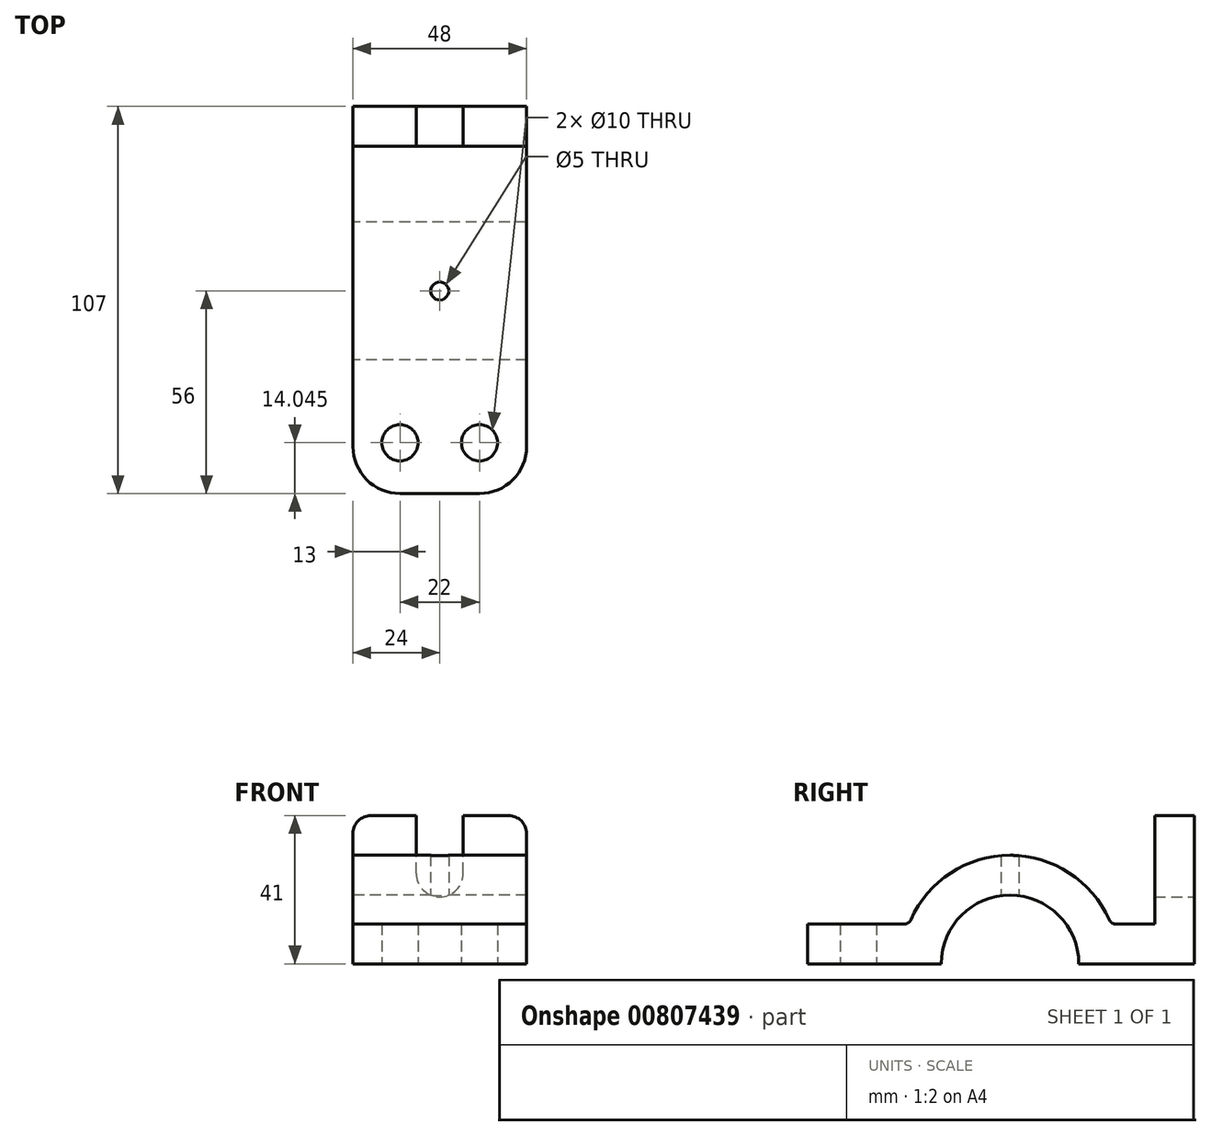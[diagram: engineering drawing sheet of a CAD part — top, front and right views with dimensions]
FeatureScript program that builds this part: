
annotation { "Feature Type Name" : "Feature", "Feature Type Description" : "" }
export const myFeature = defineFeature(function(context is Context, id is Id, definition is map)
    precondition{}
    {
        {
            var Q0;
            Q0=qCreatedBy(makeId("Right.planeOp"),FACE);
            var sketch = newSketch(context, id + "F0", { "sketchPlane" : qUnion([Q0])});
            skCircle(sketch, "E0", {"center": v(0, 0) * mm, "radius": 19 * mm});
            skCircle(sketch, "E1", {"center": v(0, 0) * mm, "radius": 30 * mm});
            skLineSegment(sketch, "E2.bottom", {"start": v(-56, 0) * mm, "end": v(51, 0) * mm});
            skLineSegment(sketch, "E2.top", {"start": v(-56, 11) * mm, "end": v(51, 11) * mm});
            skLineSegment(sketch, "E2.left", {"start": v(-56, 0) * mm, "end": v(-56, 11) * mm});
            skLineSegment(sketch, "E2.right", {"start": v(51, 0) * mm, "end": v(51, 11) * mm});
            skLineSegment(sketch, "E3.bottom", {"start": v(51, 11) * mm, "end": v(40, 11) * mm});
            skLineSegment(sketch, "E3.top", {"start": v(51, 41) * mm, "end": v(40, 41) * mm});
            skLineSegment(sketch, "E3.left", {"start": v(51, 11) * mm, "end": v(51, 41) * mm});
            skLineSegment(sketch, "E3.right", {"start": v(40, 11) * mm, "end": v(40, 41) * mm});
            skSolve(sketch);
        }
        {
            var Q0;
            {var subQ5=sQuery(id+"F0.wireOp",EDGE,"E2.left");Q0=makeQuery(id+"F0.imprint","IMPRINT",FACE,{"disambiguationData":[TD([[makeQuery(id+"F0.imprint","IMPRINT",EDGE,{"derivedFrom":subQ5}),-1.0]])]});}
            var Q1;
            {var subQ0=sQuery(id+"F0.wireOp",EDGE,"E2.bottom");var subQ1=sQuery(id+"F0.wireOp",EDGE,"E0");var subQ2=makeQuery(id+"F0.imprint","INTERSECT",VERTEX,{"disambiguationData":[OD(0.0)],"derivedFrom":[subQ1,subQ0]});Q1=makeQuery(id+"F0.imprint","IMPRINT",FACE,{"disambiguationData":[TD([[makeQuery(id+"F0.imprint","IMPRINT",EDGE,{"disambiguationData":[TD([[subQ2,1.0]])],"derivedFrom":subQ1}),-1.0]])]});}
            var Q2;
            {var subQ0=sQuery(id+"F0.wireOp",EDGE,"E2.top");var subQ1=sQuery(id+"F0.wireOp",EDGE,"E0");var subQ2=makeQuery(id+"F0.imprint","INTERSECT",VERTEX,{"disambiguationData":[OD(0.0)],"derivedFrom":[subQ1,subQ0]});Q2=makeQuery(id+"F0.imprint","IMPRINT",FACE,{"disambiguationData":[TD([[makeQuery(id+"F0.imprint","IMPRINT",EDGE,{"disambiguationData":[TD([[subQ2,1.0]])],"derivedFrom":subQ1}),-1.0]])]});}
            var Q3;
            {var subQ0=sQuery(id+"F0.wireOp",EDGE,"E2.top");var subQ1=sQuery(id+"F0.wireOp",EDGE,"E0");var subQ2=makeQuery(id+"F0.imprint","INTERSECT",VERTEX,{"disambiguationData":[OD(1.0)],"derivedFrom":[subQ1,subQ0]});Q3=makeQuery(id+"F0.imprint","IMPRINT",FACE,{"disambiguationData":[TD([[makeQuery(id+"F0.imprint","IMPRINT",EDGE,{"disambiguationData":[TD([[subQ2,1.0]])],"derivedFrom":subQ1}),-1.0]])]});}
            var Q4;
            {var subQ0=sQuery(id+"F0.wireOp",EDGE,"E2.right");Q4=makeQuery(id+"F0.imprint","IMPRINT",FACE,{"disambiguationData":[TD([[makeQuery(id+"F0.imprint","IMPRINT",EDGE,{"derivedFrom":subQ0}),1.0]])]});}
            var Q5;
            Q5=makeQuery(id+"F0.imprint","IMPRINT",FACE,{"disambiguationData":[TD([[makeQuery(id+"F0.imprint","IMPRINT",EDGE,{"derivedFrom":sQuery(id+"F0.wireOp",EDGE,"E3.top")}),1.0]])]});
            extrude(context, id + "F1", {"entities" : qUnion([Q0, Q1, Q2, Q3, Q4, Q5]), "endBound" : BoundingType.SYMMETRIC, "depth" : 48 * mm, "offsetDistance" : 25 * mm});
        }
        {
            var Q0;
            Q0=makeQuery(id+"F1.opExtrude","SWEPT_FACE",FACE,{"disambiguationData":[OSD([sQuery(id+"F0.wireOp",EDGE,"E2.right"),sQuery(id+"F0.wireOp",EDGE,"E3.left")])]});
            var sketch = newSketch(context, id + "F2", { "sketchPlane" : qUnion([Q0])});
            skLineSegment(sketch, "E4", {"start": v(0, 0) * mm, "end": v(0, 41) * mm, "construction": true});
            skCircle(sketch, "E5", {"center": v(0, 25) * mm, "radius": 6.5 * mm});
            skLineSegment(sketch, "E6", {"start": v(-6.5, 25) * mm, "end": v(-6.5, 41) * mm});
            skLineSegment(sketch, "E7", {"start": v(6.5, 25) * mm, "end": v(6.5, 41) * mm});
            skSolve(sketch);
        }
        {
            var Q0;
            {var subQ0=sQuery(id+"F2.wireOp",EDGE,"E5");var subQ2=makeQuery(id+"F2.imprint","INTERSECT",VERTEX,{"derivedFrom":[subQ0,sQuery(id+"F2.wireOp",EDGE,"E6")]});Q0=makeQuery(id+"F2.imprint","IMPRINT",FACE,{"disambiguationData":[TD([[makeQuery(id+"F2.imprint","IMPRINT",EDGE,{"disambiguationData":[TD([[subQ2,1.0]])],"derivedFrom":subQ0}),1.0]])]});}
            var Q1;
            {var subQ2=sQuery(id+"F2.wireOp",EDGE,"E6");Q1=makeQuery(id+"F2.imprint","IMPRINT",FACE,{"disambiguationData":[TD([[makeQuery(id+"F2.imprint","IMPRINT",EDGE,{"derivedFrom":subQ2}),-1.0]])]});}
            var Q2;
            Q2=makeQuery(id+"F1.opExtrude","SWEPT_FACE",FACE,{"disambiguationData":[OSD([sQuery(id+"F0.wireOp",EDGE,"E3.right")])]});
            extrude(context, id + "F3", {"entities" : qUnion([Q0, Q1]), "operationType" : NewBodyOperationType.REMOVE, "endBound" : BoundingType.UP_TO_SURFACE, "oppositeDirection" : true, "endBoundEntityFace" : qUnion([Q2]), "depth" : 25 * mm});
        }
        {
            var Q0;
            Q0=qCreatedBy(makeId("Top.planeOp"),FACE);
            var sketch = newSketch(context, id + "F4", { "sketchPlane" : qUnion([Q0])});
            skCircle(sketch, "E8", {"center": v(0, 0) * mm, "radius": 2.5 * mm});
            skLineSegment(sketch, "E9", {"start": v(24, -41.96) * mm, "end": v(-24, -41.96) * mm, "construction": true});
            skLineSegment(sketch, "E10", {"start": v(0, -56) * mm, "end": v(0, -27.91) * mm, "construction": true});
            skCircle(sketch, "E11", {"center": v(-11, -41.96) * mm, "radius": 5 * mm});
            skCircle(sketch, "E12", {"center": v(11, -41.96) * mm, "radius": 5 * mm});
            skSolve(sketch);
        }
        {
            var Q0;
            Q0=qSketchRegion(id+"F4",true);
            extrude(context, id + "F5", {"entities" : qUnion([Q0]), "operationType" : NewBodyOperationType.REMOVE, "endBound" : BoundingType.THROUGH_ALL, "depth" : 25 * mm});
        }
        {
            var Q0;
            Q0=makeQuery(id+"F1.opExtrude","CAP_EDGE",EDGE,{"disambiguationData":[OSD([sQuery(id+"F0.wireOp",EDGE,"E2.left")])],"isStart":false});
            var Q1;
            Q1=makeQuery(id+"F1.opExtrude","CAP_EDGE",EDGE,{"disambiguationData":[OSD([sQuery(id+"F0.wireOp",EDGE,"E2.left")])],"isStart":true});
            fillet(context, id + "F6", {"entities" : qUnion([Q0, Q1]), "radius" : 13 * mm, "tangentPropagation" : true, "allowEdgeOverflow" : false});
        }
        {
            var Q0;
            Q0=makeQuery(id+"F1.opExtrude","CAP_EDGE",EDGE,{"disambiguationData":[OSD([sQuery(id+"F0.wireOp",EDGE,"E3.top")])],"isStart":false});
            var Q1;
            Q1=makeQuery(id+"F1.opExtrude","CAP_EDGE",EDGE,{"disambiguationData":[OSD([sQuery(id+"F0.wireOp",EDGE,"E3.top")])],"isStart":true});
            fillet(context, id + "F7", {"entities" : qUnion([Q0, Q1]), "radius" : 5 * mm, "tangentPropagation" : true, "allowEdgeOverflow" : false});
        }
        {
            var Q0;
            {var subQ0=sQuery(id+"F0.wireOp",EDGE,"E2.top");var subQ1=sQuery(id+"F0.wireOp",EDGE,"E1");Q0=makeQuery(id+"F1.opExtrude","SWEPT_EDGE",EDGE,{"disambiguationData":[OSD([subQ1,subQ0]),TDD([makeQuery(id+"F0.imprint","INTERSECT",VERTEX,{"disambiguationData":[OD(1.0)],"derivedFrom":[subQ1,subQ0]})])]});}
            var Q1;
            {var subQ0=sQuery(id+"F0.wireOp",EDGE,"E2.top");var subQ1=sQuery(id+"F0.wireOp",EDGE,"E1");Q1=makeQuery(id+"F1.opExtrude","SWEPT_EDGE",EDGE,{"disambiguationData":[OSD([subQ1,subQ0]),TDD([makeQuery(id+"F0.imprint","INTERSECT",VERTEX,{"disambiguationData":[OD(0.0)],"derivedFrom":[subQ1,subQ0]})])]});}
            fillet(context, id + "F8", {"entities" : qUnion([Q0, Q1]), "radius" : 2 * mm, "tangentPropagation" : true, "allowEdgeOverflow" : false});
        }
    });
